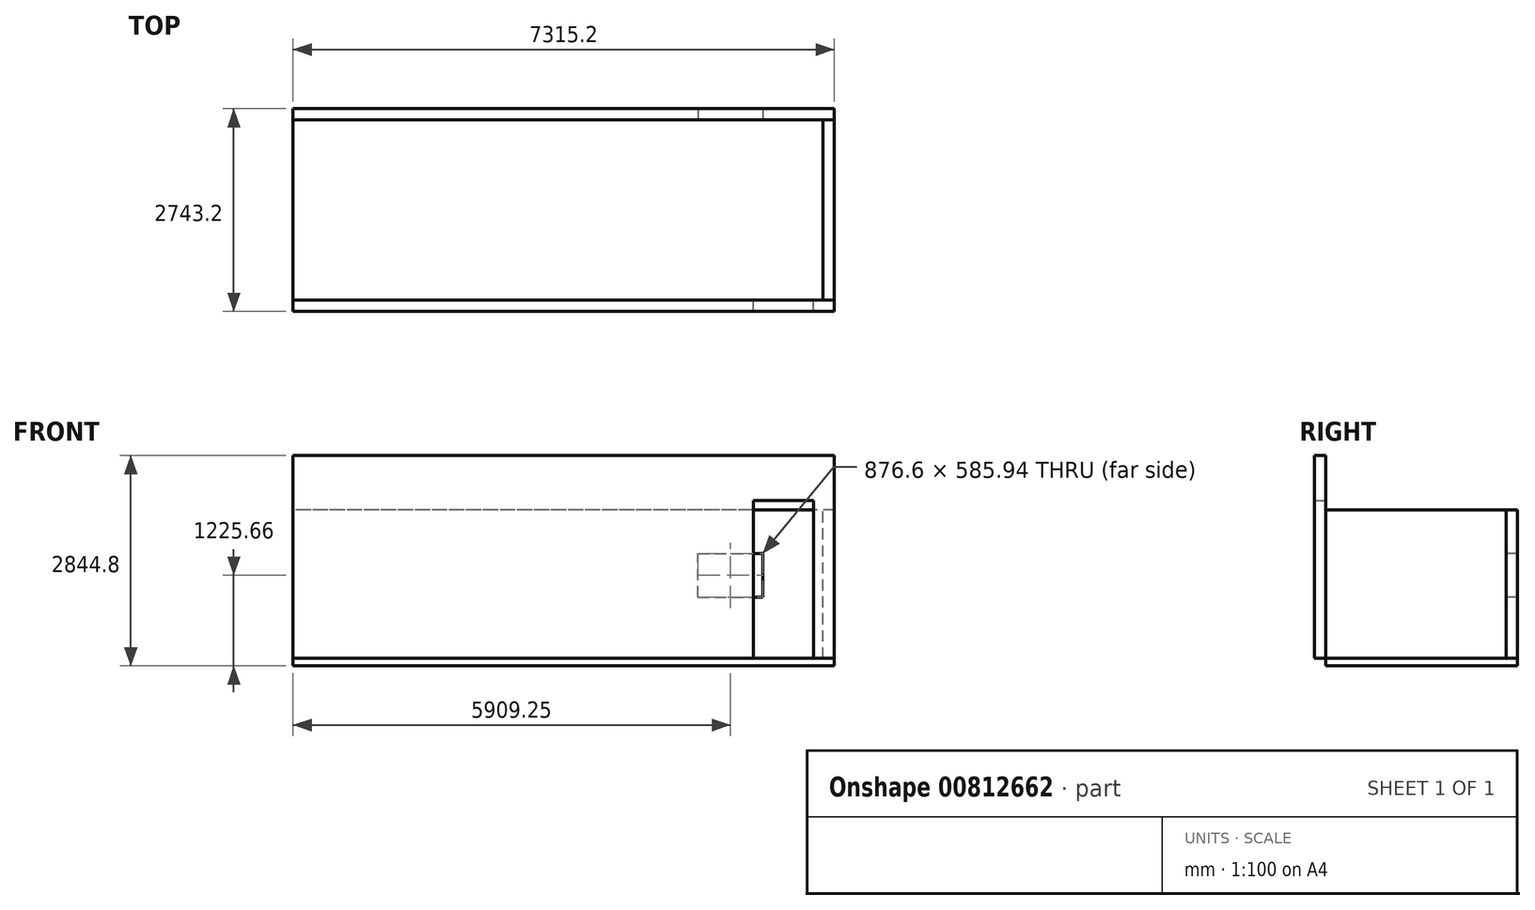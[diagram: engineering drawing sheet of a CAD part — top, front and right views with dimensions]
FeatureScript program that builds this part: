
annotation { "Feature Type Name" : "Feature", "Feature Type Description" : "" }
export const myFeature = defineFeature(function(context is Context, id is Id, definition is map)
    precondition{}
    {
        {
            var Q0;
            Q0=qCreatedBy(makeId("Front.planeOp"),FACE);
            var sketch = newSketch(context, id + "F0", { "sketchPlane" : qUnion([Q0])});
            skLineSegment(sketch, "E0.bottom", {"start": v(0, 0) * mm, "end": v(-7315.2, 0) * mm});
            skLineSegment(sketch, "E0.top", {"start": v(0, 2006.6) * mm, "end": v(-7315.2, 2006.6) * mm});
            skLineSegment(sketch, "E0.left", {"start": v(0, 0) * mm, "end": v(0, 2006.6) * mm});
            skLineSegment(sketch, "E0.right", {"start": v(-7315.2, 0) * mm, "end": v(-7315.2, 2006.6) * mm});
            skSolve(sketch);
        }
        {
            var Q0;
            Q0 = qSketchRegion(id + "F0", true);
            extrude(context, id + "F1", {"entities" : qUnion([Q0]), "depth" : 152.4 * mm, "offsetDistance" : 25.4 * mm});
        }
        {
            var Q0;
            Q0=makeQuery(id+"F1.opExtrude","CAP_FACE",FACE,{"disambiguationData":[OSD([sQuery(id+"F0.wireOp",EDGE,"E0.bottom"),sQuery(id+"F0.wireOp",EDGE,"E0.top"),sQuery(id+"F0.wireOp",EDGE,"E0.left"),sQuery(id+"F0.wireOp",EDGE,"E0.right")])],"isStart":false});
            var sketch = newSketch(context, id + "F2", { "sketchPlane" : qUnion([Q0])});
            skLineSegment(sketch, "E1.bottom", {"start": v(-1844.25, 831.09) * mm, "end": v(-967.65, 831.09) * mm});
            skLineSegment(sketch, "E1.top", {"start": v(-1844.25, 1417.03) * mm, "end": v(-967.65, 1417.03) * mm});
            skLineSegment(sketch, "E1.left", {"start": v(-1844.25, 831.09) * mm, "end": v(-1844.25, 1417.03) * mm});
            skLineSegment(sketch, "E1.right", {"start": v(-967.65, 831.09) * mm, "end": v(-967.65, 1417.03) * mm});
            skSolve(sketch);
        }
        {
            var Q0;
            Q0 = qSketchRegion(id + "F2", true);
            extrude(context, id + "F3", {"entities" : qUnion([Q0]), "operationType" : NewBodyOperationType.REMOVE, "endBound" : BoundingType.THROUGH_ALL, "oppositeDirection" : true, "depth" : 25.4 * mm, "offsetDistance" : 25.4 * mm});
        }
        {
            var Q0;
            Q0=makeQuery(id+"F1.opExtrude","CAP_FACE",FACE,{"disambiguationData":[OSD([sQuery(id+"F0.wireOp",EDGE,"E0.bottom"),sQuery(id+"F0.wireOp",EDGE,"E0.top"),sQuery(id+"F0.wireOp",EDGE,"E0.left"),sQuery(id+"F0.wireOp",EDGE,"E0.right")])],"isStart":false});
            var sketch = newSketch(context, id + "F4", { "sketchPlane" : qUnion([Q0])});
            skLineSegment(sketch, "E2.bottom", {"start": v(0, 0) * mm, "end": v(-152.4, 0) * mm});
            skLineSegment(sketch, "E2.top", {"start": v(0, 2006.6) * mm, "end": v(-152.4, 2006.6) * mm});
            skLineSegment(sketch, "E2.left", {"start": v(0, 0) * mm, "end": v(0, 2006.6) * mm});
            skLineSegment(sketch, "E2.right", {"start": v(-152.4, 0) * mm, "end": v(-152.4, 2006.6) * mm});
            skSolve(sketch);
        }
        {
            var Q0;
            Q0 = qSketchRegion(id + "F4", true);
            extrude(context, id + "F5", {"entities" : qUnion([Q0]), "depth" : 2438.4 * mm, "offsetDistance" : 25.4 * mm});
        }
        {
            var Q0;
            Q0=makeQuery(id+"F1.opExtrude","SWEPT_FACE",FACE,{"disambiguationData":[OSD([sQuery(id+"F0.wireOp",EDGE,"E0.bottom")])]});
            var sketch = newSketch(context, id + "F6", { "sketchPlane" : qUnion([Q0])});
            skLineSegment(sketch, "E3.bottom", {"start": v(0, 0) * mm, "end": v(-7315.2, 0) * mm});
            skLineSegment(sketch, "E3.top", {"start": v(0, 2590.8) * mm, "end": v(-7315.2, 2590.8) * mm});
            skLineSegment(sketch, "E3.left", {"start": v(0, 0) * mm, "end": v(0, 2590.8) * mm});
            skLineSegment(sketch, "E3.right", {"start": v(-7315.2, 0) * mm, "end": v(-7315.2, 2590.8) * mm});
            skSolve(sketch);
        }
        {
            var Q0;
            Q0 = qSketchRegion(id + "F6", true);
            extrude(context, id + "F7", {"entities" : qUnion([Q0]), "depth" : 101.6 * mm, "offsetDistance" : 25.4 * mm});
        }
        {
            var Q0;
            Q0=makeQuery(id+"F5.opExtrude","CAP_FACE",FACE,{"disambiguationData":[OSD([sQuery(id+"F4.wireOp",EDGE,"E2.bottom"),sQuery(id+"F4.wireOp",EDGE,"E2.top"),sQuery(id+"F4.wireOp",EDGE,"E2.left"),sQuery(id+"F4.wireOp",EDGE,"E2.right")])],"isStart":false});
            var sketch = newSketch(context, id + "F8", { "sketchPlane" : qUnion([Q0])});
            skLineSegment(sketch, "E4.bottom", {"start": v(0, 0) * mm, "end": v(-7315.2, 0) * mm});
            skLineSegment(sketch, "E4.top", {"start": v(0, 2743.2) * mm, "end": v(-7315.2, 2743.2) * mm});
            skLineSegment(sketch, "E4.left", {"start": v(0, 0) * mm, "end": v(0, 2743.2) * mm});
            skLineSegment(sketch, "E4.right", {"start": v(-7315.2, 0) * mm, "end": v(-7315.2, 2743.2) * mm});
            skPoint(sketch, "E5.orphan", {"position": v(0, 3433.12) * mm});
            skSolve(sketch);
        }
        {
            var Q0;
            Q0 = qSketchRegion(id + "F8", true);
            extrude(context, id + "F9", {"entities" : qUnion([Q0]), "depth" : 152.4 * mm, "offsetDistance" : 25.4 * mm});
        }
        {
            var Q0;
            Q0=makeQuery(id+"F9.opExtrude","CAP_FACE",FACE,{"disambiguationData":[OSD([sQuery(id+"F8.wireOp",EDGE,"E4.bottom"),sQuery(id+"F8.wireOp",EDGE,"E4.top"),sQuery(id+"F8.wireOp",EDGE,"E4.left"),sQuery(id+"F8.wireOp",EDGE,"E4.right")])],"isStart":true});
            var sketch = newSketch(context, id + "F10", { "sketchPlane" : qUnion([Q0])});
            skLineSegment(sketch, "E6.bottom", {"start": v(279.4, 0) * mm, "end": v(1092.2, 0) * mm});
            skLineSegment(sketch, "E6.top", {"start": v(279.4, 2133.6) * mm, "end": v(1092.2, 2133.6) * mm});
            skLineSegment(sketch, "E6.left", {"start": v(279.4, 0) * mm, "end": v(279.4, 2133.6) * mm});
            skLineSegment(sketch, "E6.right", {"start": v(1092.2, 0) * mm, "end": v(1092.2, 2133.6) * mm});
            skSolve(sketch);
        }
        {
            var Q0;
            Q0 = qSketchRegion(id + "F10", true);
            extrude(context, id + "F11", {"entities" : qUnion([Q0]), "operationType" : NewBodyOperationType.REMOVE, "endBound" : BoundingType.THROUGH_ALL, "oppositeDirection" : true, "depth" : 25.4 * mm, "offsetDistance" : 25.4 * mm});
        }
    });
